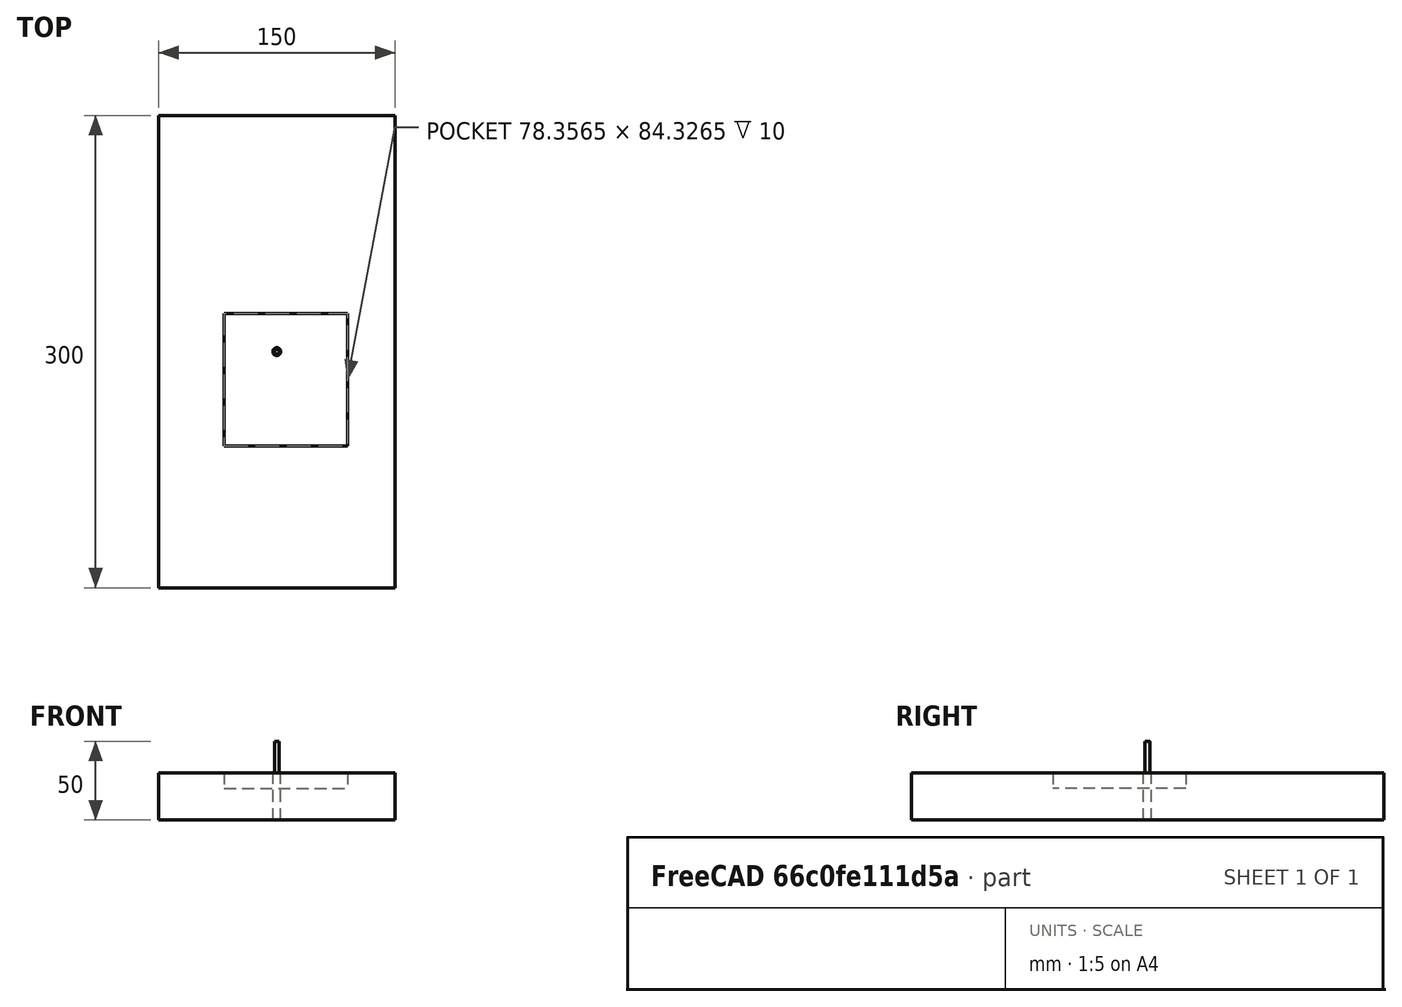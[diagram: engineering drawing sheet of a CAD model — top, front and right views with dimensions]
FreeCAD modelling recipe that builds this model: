
FCSTD DOCUMENT  (FreeCAD 0.19R24291 (Git))
Label: supportPortiqueVideo
License: All rights reserved
LicenseURL: http://en.wikipedia.org/wiki/All_rights_reserved
objects: Part::FeaturePython×3, Path::FeaturePython×3, Sketcher::SketchObject×2, App::DocumentObjectGroup×2, PartDesign::Pad×1, PartDesign::Pocket×1, PartDesign::Body×1, App::FeaturePython×1, Path::FeatureCompoundPython×1, Mesh::FeaturePython×1
note: 11 computed .brp shape members not serialized (recipe doc carries the construction recipe); baked Part::Feature solids carry a one-line shape summary decoded from their .brp

FEATURE [Sketcher::SketchObject] Sketch
  FullyConstrained = false
  MapMode = 5
  Support = -> [XY_Plane]
  sketch-geometry (4):
    g0: LineSegment StartX=-75 StartY=150 StartZ=0 EndX=75 EndY=150 EndZ=0
    g1: LineSegment StartX=75 StartY=150 StartZ=0 EndX=75 EndY=-150 EndZ=0
    g2: LineSegment StartX=75 StartY=-150 StartZ=0 EndX=-75 EndY=-150 EndZ=0
    g3: LineSegment StartX=-75 StartY=-150 StartZ=0 EndX=-75 EndY=150 EndZ=0
  constraints (10):
    c: Coincident(g0,g1)
    c: Coincident(g1,g2)
    c: Coincident(g2,g3)
    c: Coincident(g3,g0)
    c: Horizontal(g2)
    c: Vertical(g1)
    c: DistanceY(g1,g1) = 300
    c: DistanceX(g0,g0) = 150
    c: Symmetric(g0,g2,g-1)
    c: Symmetric(g0,g0,g-2)
FEATURE [PartDesign::Pad] Pad
  AllowMultiFace = false
  Direction = (1,1,1)
  Length = 30
  Length2 = 100
  Profile = -> Sketch
  Type = 0
FEATURE [Sketcher::SketchObject] Sketch002
  AttachmentOffset = pos=(0,0,30) rot=(0,0,1;0rad)
  FullyConstrained = false
  MapMode = 5
  Placement = pos=(0,0,30) rot=(0,0,1;0rad)
  Support = -> [XY_Plane]
  sketch-geometry (4):
    g0: LineSegment StartX=-33.4074 StartY=24.2688 StartZ=0 EndX=44.9491 EndY=24.2688 EndZ=0
    g1: LineSegment StartX=44.9491 StartY=24.2688 StartZ=0 EndX=44.9491 EndY=-60.0577 EndZ=0
    g2: LineSegment StartX=44.9491 StartY=-60.0577 StartZ=0 EndX=-33.4074 EndY=-60.0577 EndZ=0
    g3: LineSegment StartX=-33.4074 StartY=-60.0577 StartZ=0 EndX=-33.4074 EndY=24.2688 EndZ=0
  constraints (8):
    c: Coincident(g0,g1)
    c: Coincident(g1,g2)
    c: Coincident(g2,g3)
    c: Coincident(g3,g0)
    c: Horizontal(g0)
    c: Horizontal(g2)
    c: Vertical(g1)
    c: Vertical(g3)
FEATURE [PartDesign::Pocket] Pocket
  BaseFeature = -> Pad
  Length = 10
  Length2 = 100
  Profile = -> Sketch002
  Type = 0
FEATURE [PartDesign::Body] Body
  Group = -> [Sketch,Pad,Sketch002,Pocket]
  Origin = -> Origin
  Tip = -> Pocket
FEATURE [App::FeaturePython] SetupSheet  # Path/CAM operation (typed FeaturePython)
  ClearanceHeightExpression = OpStockZMax+SetupSheet.ClearanceHeightOffset
  ClearanceHeightOffset = 5
  CoolantMode = 0
  CoolantModes = None | Flood | Mist
  FinalDepthExpression = OpFinalDepth
  HorizRapid = 0
  SafeHeightExpression = OpStockZMax+SetupSheet.SafeHeightOffset
  SafeHeightOffset = 3
  StartDepthExpression = OpStartDepth
  StepDownExpression = OpToolDiameter
  VertRapid = 0
FEATURE [Part::FeaturePython] Clone  label="Model-Body"  # Draft clone (typed FeaturePython)
  AttacherType = Attacher::AttachEngine3D
  Fuse = false
  Objects = -> [Body]
  PathResource = Model
  Scale = (1,1,1)
FEATURE [App::DocumentObjectGroup] Model
  Group = -> [Clone]
FEATURE [Part::FeaturePython] Stock001  # WARN: FeaturePython — macro-defined, semantics opaque (R4)
  Height = 30
  Length = 150
  Placement = pos=(-75,-150,0) rot=(0,0,1;0rad)
  StockType = CreateBox
  Width = 300
FEATURE [Part::FeaturePython] ToolBit001  label="5mm Endmill"  # Path/CAM toolbit (typed FeaturePython)
  BitPropertyNames = Chipload | CuttingEdgeHeight | Diameter | Flutes | Length | Material | ShankDiameter
  BitShape = D:/Program Files/FreeCAD 0.19/Mod\Path\Tools\Shape\endmill.fcstd
  Chipload = 0
  CuttingEdgeHeight = 30
  Diameter = 5
  File = <userpath>/AppData/Roaming/FreeCAD/Macro\Bit\5mm_Endmill.fctb
  Flutes = 0
  Length = 50
  Material = 0
  ShankDiameter = 3
  ShapeName = endmill
FEATURE [Path::FeaturePython] TC__5mm_Endmill  label="TC: 5mm Endmill"  # Path/CAM operation (typed FeaturePython)
  HorizFeed = 0
  HorizRapid = 0
  SpindleDir = 0
  SpindleSpeed = 0
  Tool = -> ToolBit001
  ToolNumber = 1
  VertFeed = 0
  VertRapid = 0
  expr: HorizRapid = SetupSheet.HorizRapid
  expr: VertRapid = SetupSheet.VertRapid
FEATURE [App::DocumentObjectGroup] Tools
  Group = -> [TC__5mm_Endmill]
FEATURE [Path::FeaturePython] Profile  # Path/CAM operation (typed FeaturePython)
  Active = true
  AreaParams:
    Tolerance = 1e-07
    FitArcs = True
    Simplify = False
    CleanDistance = 0.0
    Accuracy = 0.01
    Unit = 1.0
    MinArcPoints = 4
    MaxArcPoints = 100
    ClipperScale = 10000000.0
    Fill = 0
    Coplanar = 0
    Reorient = True
    Outline = False
    Explode = False
    OpenMode = 0
    Deflection = 0.01
    SubjectFill = 0
    ClipFill = 0
    Offset = 2.5
    ExtraPass = 0
    Stepover = 0.0
    LastStepover = 0.0
    JoinType = 0
    EndType = 0
    MiterLimit = 2.0
    RoundPrecision = 0.0
    PocketMode = 0
    ToolRadius = 1.0
    PocketExtraOffset = 0.0
    PocketStepover = 0.0
    PocketLastStepover = 0.0
    FromCenter = False
    Angle = 45.0
    AngleShift = 0.0
    Shift = 0.0
    Thicken = False
    SectionCount = -1
    Stepdown = 1.0
    SectionOffset = 0.0
    SectionTolerance = 1e-06
    SectionMode = 2
    Project = False
  AttemptInverseAngle = true
  ClearanceHeight = 35
  CoolantMode = None
  CycleTime = Erreur de temps de cycle
  Direction = 0
  EnableRotation = 0
  FinalDepth = 0.1
  HandleMultipleFeatures = 0
  InverseAngle = false
  JoinType = 0
  LimitDepthToFace = true
  MiterLimit = 0.1
  OffsetExtra = 0
  OpFinalDepth = 0
  OpStartDepth = 30
  OpStockZMax = 30
  OpStockZMin = 0
  OpToolDiameter = 5
  PathParams = {'orientation': 1, 'feedrate': 0.0, 'feedrate_v': 0.0, 'verbose': True, 'resume_height': 33.0, 'retraction': 35.0, 'return_end': True, 'preamble': False}
  ReverseDirection = false
  SafeHeight = 33
  Side = 0
  StartDepth = 30
  StartPoint = (0,0,0)
  StepDown = 2
  ToolController = -> TC__5mm_Endmill
  UseComp = true
  UseStartPoint = false
  processCircles = false
  processHoles = false
  processPerimeter = true
  expr: ClearanceHeight = OpStockZMax + SetupSheet.ClearanceHeightOffset
  expr: SafeHeight = OpStockZMax + SetupSheet.SafeHeightOffset
  expr: StepDown = 2
  expr: FinalDepth = 0.1
  expr: StartDepth = OpStartDepth
FEATURE [Path::FeatureCompoundPython] Operations  # Path/CAM operation (typed FeaturePython)
  Group = -> [Profile]
  UsePlacements = false
FEATURE [Path::FeaturePython] Job  label="ok"  # Path/CAM operation (typed FeaturePython)
  CycleTime = 00:00:00
  GeometryTolerance = 0
  LastPostProcessDate = 2021-10-09 01:52:20.916596
  LastPostProcessOutput = <path>
  Model = -> Model
  Operations = -> Operations
  OrderOutputBy = 0
  PostProcessor = 0
  SetupSheet = -> SetupSheet
  SplitOutput = false
  Stock = -> Stock001
  Tools = -> Tools
FEATURE [Mesh::FeaturePython] CutMaterial  # WARN: FeaturePython — macro-defined, semantics opaque (R4)
note: 1 file-system path scrubbed to <path> (originals preserved in the JSON sidecar)
